# Revit family: BC_URMET_FC1719-1_LOD200
name_source: partatom
category: Appareils de communication
revit_build: Autodesk Revit 2017 (Build: 20160225_1515(x64)
units: mm (PartAtom-declared; Revit-internal decimal feet)

## family parameters
Conserver l'orientation des annotations = Non
Cote de connecteur circulaire = Utiliser le diamètre
Couper avec des vides une fois chargée = Non
Hôte = Face
Numéro OmniClass = 23.85.50.14.21
Partagée = Non
Point de calcul de pièce = Non
Titre OmniClass = Intercommunication Equipment
Type d'élément = Normal

## types (1)
- FC1719_1
    Code EAN = 8021156064120
    Commentaires du type = FC1719_1
    Description = Ce moniteur vidéo couleur 7“” est conçu pour fonctionner avec le système d’interphonie bus 2 fils 2VOICE. Son utilisation est très agréable grâce à ces 4 touches affleurantes (muni d’un guide pour les malvoyants) et une touche mécanique centrale pour la prise de la communication. La fonction renvoi d’appel vers un smartphone est compatible avec l’ajout du module Callme 1083/58. De plus, il intègre 2 télécommandes domotiques YOKIS pour un contrôle d’éclairage, volet roulant ou autre (intégrable dans YNO pour une gestion de scénario complets). La fonction Mute peut également être utilisée en mode chronométré (désactivation automatiquement après 8 heures).
    Elévation par défaut = 1219 mm
    Epaisseur Hors Tout = 23 mm  [stored 0.0754593 ft]
    Fabricant = URMET
    Largeur Hors Tout = 142 mm  [stored 0.465879 ft]
    Longueur Hors Tout = 202 mm  [stored 0.66273 ft]
    Modèle = FC1719_1
    Ouverture porte = Oui
    Réglage du volume = Oui
    Taille de l'écran  = 7"
    Voyant coupure de sonnerie = Oui

note: [stored X ft] marks values corroborated as IEEE doubles in the binary element streams (Revit-internal decimal feet)
